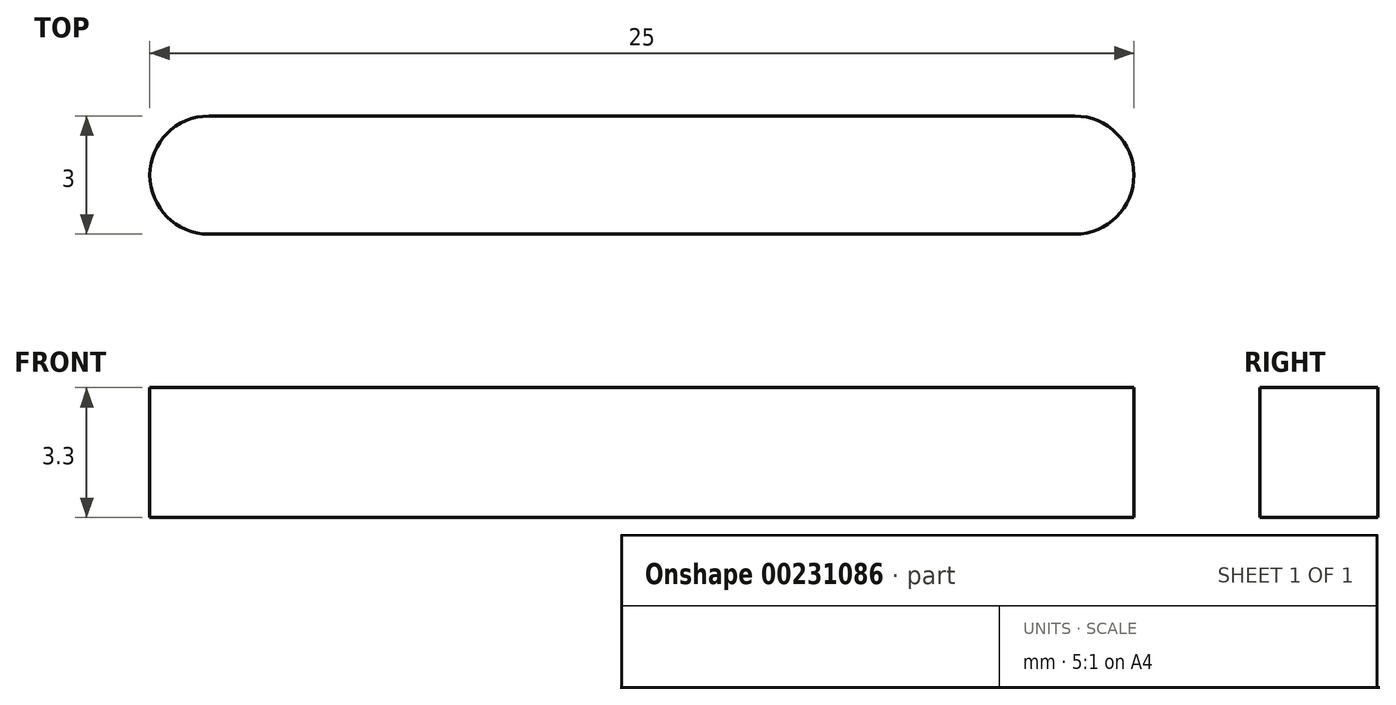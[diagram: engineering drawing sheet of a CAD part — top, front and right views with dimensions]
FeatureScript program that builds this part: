
annotation { "Feature Type Name" : "Feature", "Feature Type Description" : "" }
export const myFeature = defineFeature(function(context is Context, id is Id, definition is map)
    precondition{}
    {
        {
            var Q0;
            Q0=qCreatedBy(makeId("Top.planeOp"),FACE);
            var sketch = newSketch(context, id + "F0", { "sketchPlane" : qUnion([Q0])});
            skLineSegment(sketch, "E0.bottom", {"start": v(0, 0) * mm, "end": v(22, 0) * mm});
            skLineSegment(sketch, "E0.top", {"start": v(0, 3) * mm, "end": v(22, 3) * mm});
            skArc(sketch, "E1", {"start": v(0, 3) * mm, "mid": v(-1.5, 1.5) * mm, "end": v(0, 0) * mm});
            skArc(sketch, "E2", {"start": v(22, 0) * mm, "mid": v(23.5, 1.5) * mm, "end": v(22, 3) * mm});
            skSolve(sketch);
        }
        {
            var Q0;
            Q0 = qSketchRegion(id + "F0", true);
            extrude(context, id + "F1", {"entities" : qUnion([Q0]), "depth" : 3.3 * mm});
        }
    });
